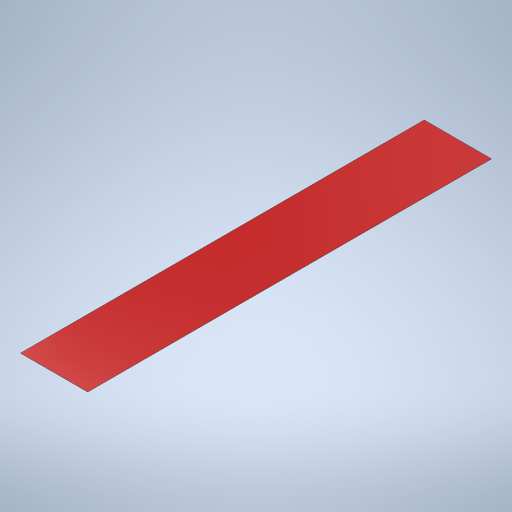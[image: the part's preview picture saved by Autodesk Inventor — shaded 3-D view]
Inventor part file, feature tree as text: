
AUTODESK INVENTOR PART (.ipt)
format: ipt  version: 2023 (Build 270158000, 158)  size: 230,912 bytes
history: native  units: in
note: dims shown in document units (in); Inventor stores cm internally (conversion verified against a paired STEP export)
features: extrude x1, sketch x1
ambient origin geometry x8: Origin, YZ Plane, XZ Plane, XY Plane, X Axis, Y Axis, Z Axis, Center Point
bodies: Solid1 (feature_tree)
feature tree (2):
  extrude  "Extrusion1"  Depth=0.1969in
  sketch  "Sketch1"  dims[d0=1.1811in d1=0.1969in d2=0.0004in d3=0.0in]
